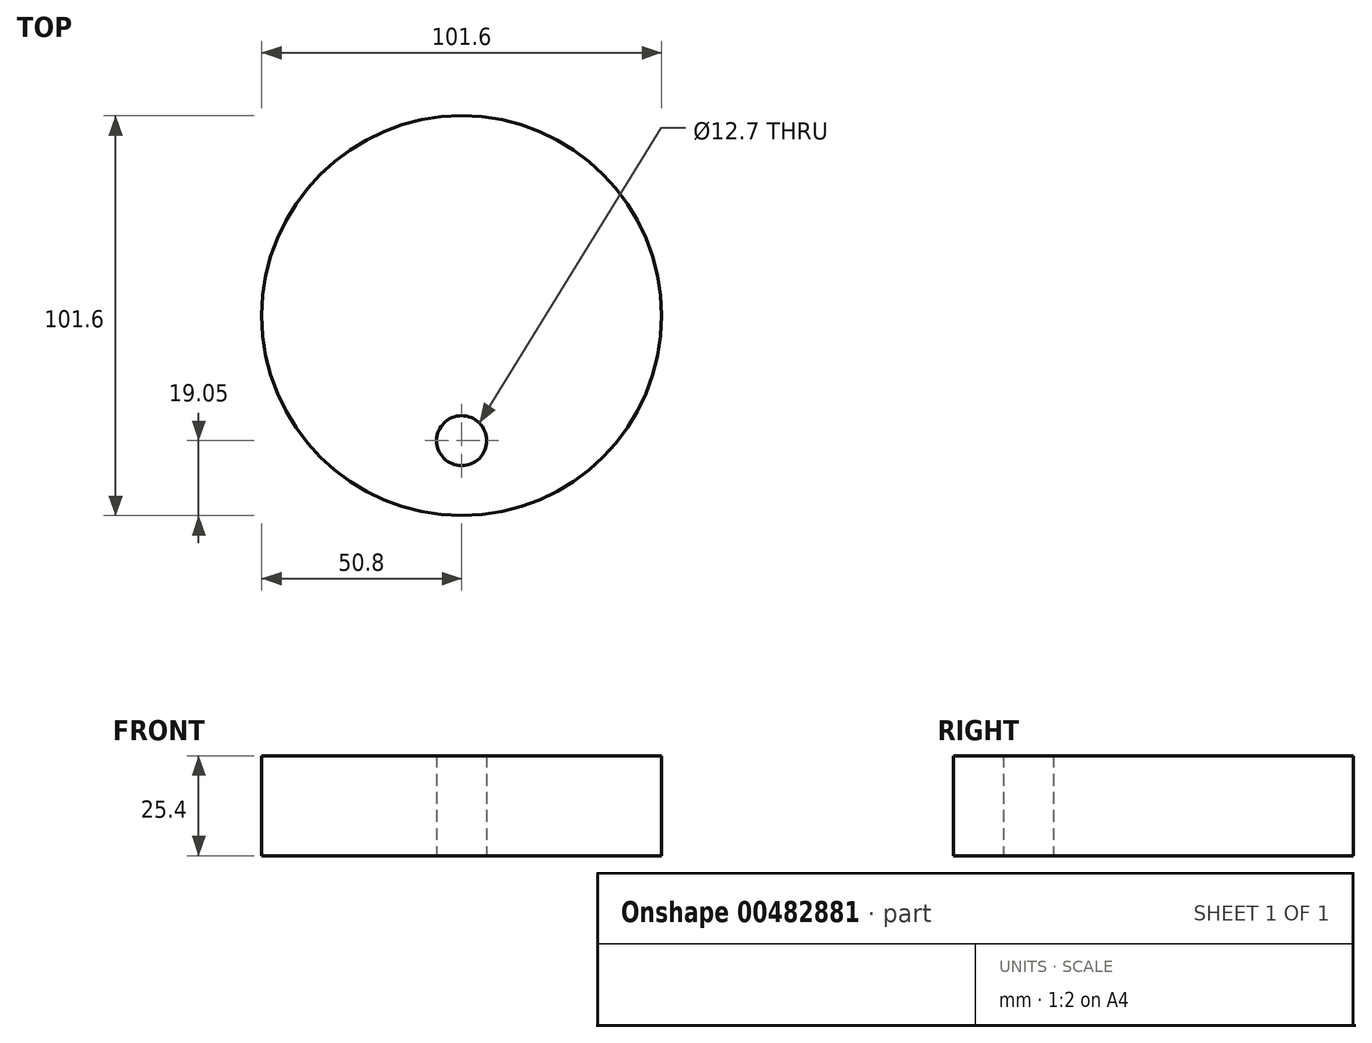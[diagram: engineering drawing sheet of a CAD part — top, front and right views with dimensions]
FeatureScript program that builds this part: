
annotation { "Feature Type Name" : "Feature", "Feature Type Description" : "" }
export const myFeature = defineFeature(function(context is Context, id is Id, definition is map)
    precondition{}
    {
        {
            var Q0;
            Q0=qCreatedBy(makeId("Top.planeOp"),FACE);
            var sketch = newSketch(context, id + "F0", { "sketchPlane" : qUnion([Q0])});
            skCircle(sketch, "E0", {"center": v(0, 0) * mm, "radius": 50.8 * mm});
            skCircle(sketch, "E1", {"center": v(0, 0) * mm, "radius": 31.75 * mm, "construction": true});
            skCircle(sketch, "E2", {"center": v(0, -31.75) * mm, "radius": 6.35 * mm});
            skSolve(sketch);
        }
        {
            var Q0;
            Q0 = qSketchRegion(id + "F0", true);
            var Q1;
            Q1=makeQuery(id+"F0.imprint","IMPRINT",FACE,{"disambiguationData":[TD([[makeQuery(id+"F0.imprint","IMPRINT",EDGE,{"derivedFrom":sQuery(id+"F0.wireOp",EDGE,"E0")}),1.0]])]});
            extrude(context, id + "F1", {"entities" : qUnion([Q0, Q1]), "depth" : 25.4 * mm});
        }
        {
            var Q0;
            Q0=makeQuery(id+"F1.opExtrude","CAP_FACE",FACE,{"disambiguationData":[OSD([sQuery(id+"F0.wireOp",EDGE,"E0"),sQuery(id+"F0.wireOp",EDGE,"E2")])],"isStart":false});
            var sketch = newSketch(context, id + "F2", { "sketchPlane" : qUnion([Q0])});
            skCircle(sketch, "E3", {"center": v(0, 0) * mm, "radius": 31.75 * mm, "construction": true});
            skSolve(sketch);
        }
    });
